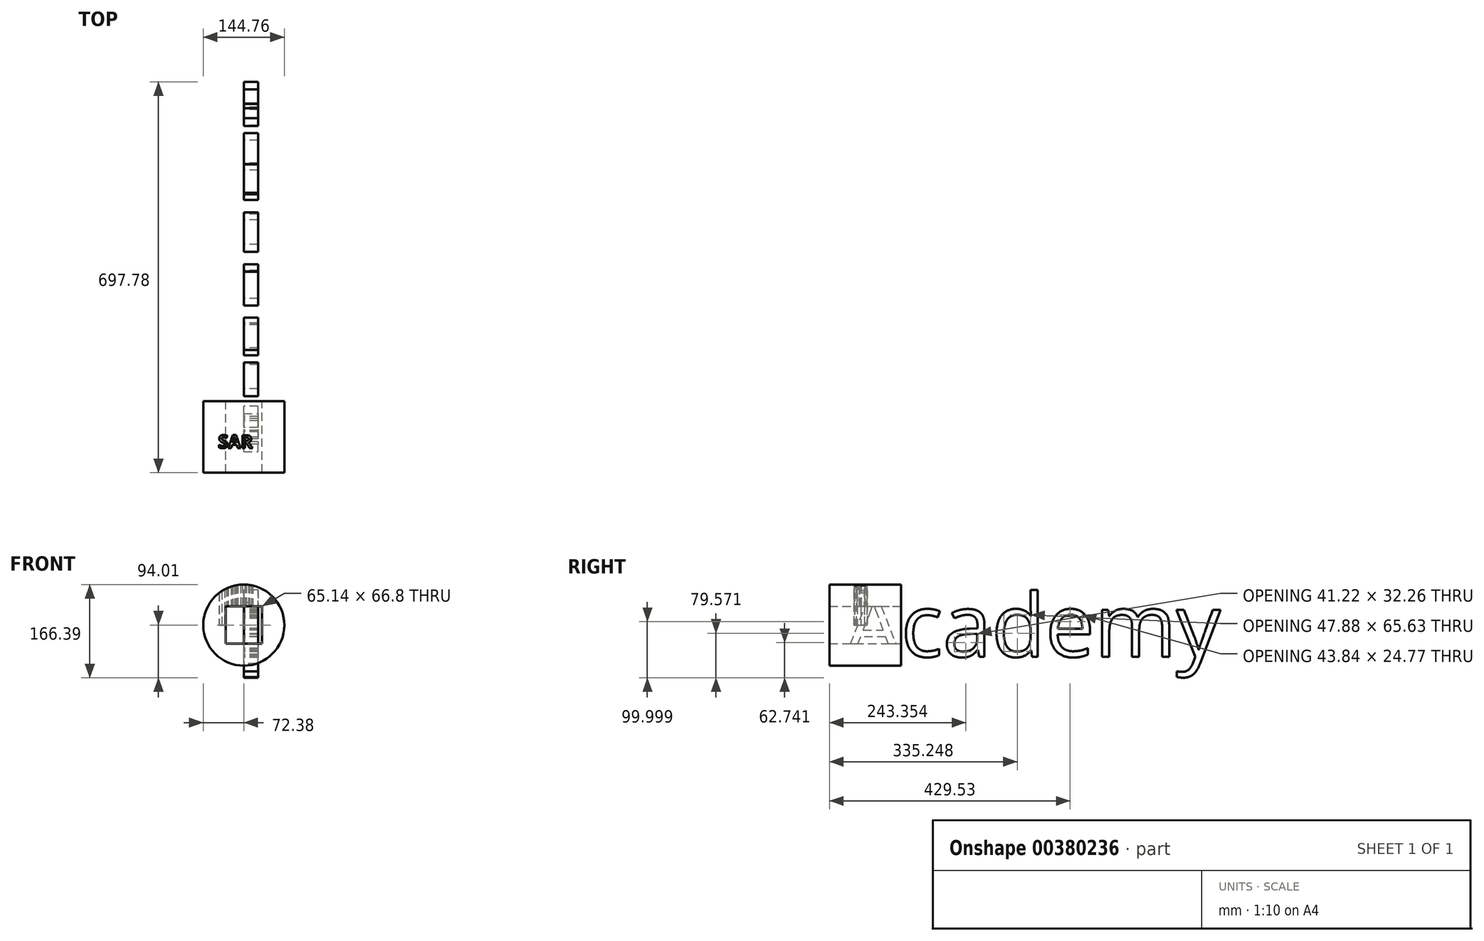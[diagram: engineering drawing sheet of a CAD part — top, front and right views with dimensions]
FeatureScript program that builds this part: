
annotation { "Feature Type Name" : "Feature", "Feature Type Description" : "" }
export const myFeature = defineFeature(function(context is Context, id is Id, definition is map)
    precondition{}
    {
        {
            var Q0;
            Q0=qCreatedBy(makeId("Front.planeOp"),FACE);
            var sketch = newSketch(context, id + "F0", { "sketchPlane" : qUnion([Q0])});
            skCircle(sketch, "E0", {"center": v(0, 0) * mm, "radius": 72.38 * mm});
            skLineSegment(sketch, "E1.bottom", {"start": v(-32.57, -33.4) * mm, "end": v(32.57, -33.4) * mm});
            skLineSegment(sketch, "E1.top", {"start": v(-32.57, 33.4) * mm, "end": v(32.57, 33.4) * mm});
            skLineSegment(sketch, "E1.left", {"start": v(-32.57, -33.4) * mm, "end": v(-32.57, 33.4) * mm});
            skLineSegment(sketch, "E1.right", {"start": v(32.57, -33.4) * mm, "end": v(32.57, 33.4) * mm});
            skSolve(sketch);
        }
        {
            var Q0;
            Q0 = qSketchRegion(id + "F0", true);
            var Q1;
            Q1=makeQuery(id+"F0.imprint","IMPRINT",FACE,{"disambiguationData":[TD([[makeQuery(id+"F0.imprint","IMPRINT",EDGE,{"derivedFrom":sQuery(id+"F0.wireOp",EDGE,"E0")}),1.0]])]});
            extrude(context, id + "F1", {"entities" : qUnion([Q0, Q1]), "depth" : 76.2 * mm, "hasSecondDirection" : true, "secondDirectionOppositeDirection" : true, "secondDirectionDepth" : 51.25 * mm});
        }
        {
            var Q0;
            Q0=qCreatedBy(makeId("Top.planeOp"),FACE);
            var sketch = newSketch(context, id + "F2", { "sketchPlane" : qUnion([Q0])});
            skText(sketch, "E2", { "text": "SAR", "fontName": "OpenSans-Bold.ttf"});
            const initialGuessF2  = {"E2": [-0.04564, -0.03236, 1, 0, 0.02324]};
            skSetInitialGuess(sketch, initialGuessF2);
            skSolve(sketch);
        }
        {
            var Q0;
            Q0 = qSketchRegion(id + "F2", true);
            extrude(context, id + "F3", {"entities" : qUnion([Q0]), "operationType" : NewBodyOperationType.REMOVE, "depth" : 150.02 * mm});
        }
        {
            var Q0;
            Q0=qCreatedBy(makeId("Right.planeOp"),FACE);
            var sketch = newSketch(context, id + "F4", { "sketchPlane" : qUnion([Q0])});
            skText(sketch, "E3", { "text": "Academy", "fontName": "OpenSans-Regular.ttf"});
            const initialGuessF4  = {"E3": [-0.0477, -0.05636, 1, 0, 0.1128]};
            skSetInitialGuess(sketch, initialGuessF4);
            skSolve(sketch);
        }
        {
            var Q0;
            Q0 = qSketchRegion(id + "F4", true);
            extrude(context, id + "F5", {"entities" : qUnion([Q0]), "operationType" : NewBodyOperationType.ADD, "depth" : 25.4 * mm});
        }
    });
